# Revit family: LBS4038A75FTT.V2,2FTT.V2,75FTB.V2,2FTB.V2
name_source: partatom
category: Plumbing Fixtures
revit_build: Autodesk Revit LT 2017 (Build: 20160225_1515(x64)
units: mm (PartAtom-declared; Revit-internal decimal feet)

## family parameters
Always vertical = Yes
Cut with Voids When Loaded = No
OmniClass Number = 23.45.05.14.17
OmniClass Title = Showers
Part Type = Normal
Room Calculation Point = No
Round Connector Dimension = Use Diameter
Shared = No
Work Plane-Based = No

## types (4) — shared parameters
Assembly Code = D2010710
Description = Trench Drain, Smooth Wall, Traditional Bull Nose Threshold
Keynote = 22 40 00.B3
Manufacturer = Best Bath Systems, Inc.
Seat Height = 18"
Type Comments = ADA Compliant
URL = http://www.best-bath.com
Unit Width = 40 1/4"

## per-type parameters (varying)
| type | Model | Threshold Height | Unit Height |
| 4LBS4038A75FTT | 4LBS4038A75FTT | 3/4" | 78 3/4" |
| 4LBS4038A2FTT | 4LBS4038A2FTT | 2" | 80" |
| 4LBS4038A75FTB | LSS24038A75FTB | 3/4" | 78 3/4" |
| 4LBS4038A2FTB | 4LBS4038A2FTB | 2" | 80" |

## geometry (parser evidence)
native form markers: Blend x41, Sweep x8
no freeform markers — native parametric forms only
